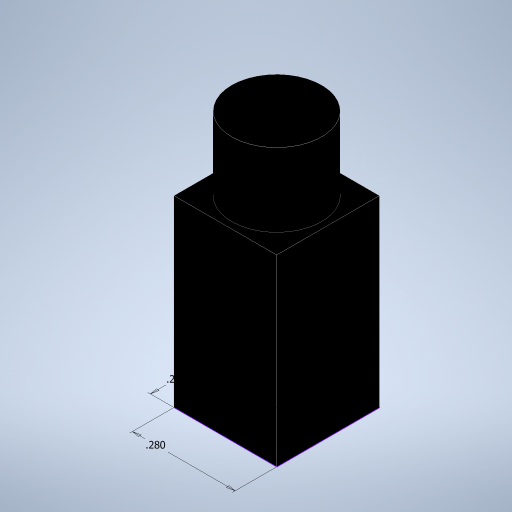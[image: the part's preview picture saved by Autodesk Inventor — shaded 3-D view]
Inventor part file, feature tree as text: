
AUTODESK INVENTOR PART (.ipt)
format: ipt  version: 2023 (Build 270158000, 158)  size: 218,624 bytes
history: native  units: in
note: dims shown in document units (in); Inventor stores cm internally (conversion verified against a paired STEP export)
features: extrude x2, sketch x1
ambient origin geometry x8: Origin, YZ Plane, XZ Plane, XY Plane, X Axis, Y Axis, Z Axis, Center Point
bodies: Solid1 (feature_tree)
feature tree (3):
  sketch  "Sketch1"  dims[d0=0.245in d1=0.14in d2=0.14in d3=0.28in d4=0.28in d5=0.7in d6=0.0in d7=0.5in d8=0.0in]
  extrude  "Extrusion1"  Depth=0.5in
  extrude  "Extrusion2"  Depth=0.5in
